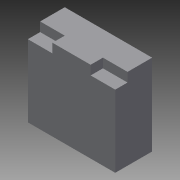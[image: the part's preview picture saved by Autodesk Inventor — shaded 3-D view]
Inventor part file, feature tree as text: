
AUTODESK INVENTOR PART (.ipt)
format: ipt  version: 2015 (Build 190159000, 159)  size: 186,880 bytes
history: native  units: in
note: dims shown in document units (in); Inventor stores cm internally (conversion verified against a paired STEP export)
features: extrude x7, sketch x7, projected_geometry x7
ambient origin geometry x8: Origin, YZ Plane, XZ Plane, XY Plane, X Axis, Y Axis, Z Axis, Center Point
bodies: Solid1 (feature_tree)
feature tree (21):
  extrude  "Extrusion1"  Depth=3.0in
  extrude  "Extrusion2"  Depth=2.0in
  extrude  "Extrusion3"  Depth=2.0in
  extrude  "Extrusion4"  Depth=0.75in TaperAngle=0.0deg
  extrude  "Extrusion5"  Depth=1.45in
  extrude  "Extrusion6"  Depth=0.5in TaperAngle=0.0deg
  extrude  "Extrusion7"  Depth=1.69in
  sketch  "Sketch1"  dims[d0=7.1in d1=3.0in]
  sketch  "Sketch2"  dims[d2=6.6in d3=0.0in d4=2.0in]
  projected_geometry  "Projected Loop1"
  sketch  "Sketch3"  dims[d5=1.0in d6=2.0in]
  projected_geometry  "Projected Loop2"
  sketch  "Sketch4"  dims[d7=1.0in d8=0.75in d9=0.0in]
  projected_geometry  "Projected Loop3"
  sketch  "Sketch5"  dims[d10=0.0625in d11=1.45in]
  projected_geometry  "Projected Loop4"
  projected_geometry  "Projected Loop5"
  sketch  "Sketch6"  dims[d12=1.45in d13=0.5in d14=0.0in]
  projected_geometry  "Projected Loop6"
  sketch  "Sketch7"  dims[d15=0.0625in d16=1.69in d17=1.69in d18=1.69in d19=1.69in d20=0.0625in d21=0.0625in d22=0.5in d23=0.0in d24=0.5in d25=0.5in d26=0.5in d27=0.5in d28=0.125in d29=0.5in d30=0.125in d31=0.5in d32=0.75in d33=0.0in d34=0.25in d35=0.25in d36=0.25in d37=1.0in d38=0.0in d39=0.25in d40=0.25in d41=0.25in d42=1.0in d43=0.0in]
  projected_geometry  "Projected Loop7"
